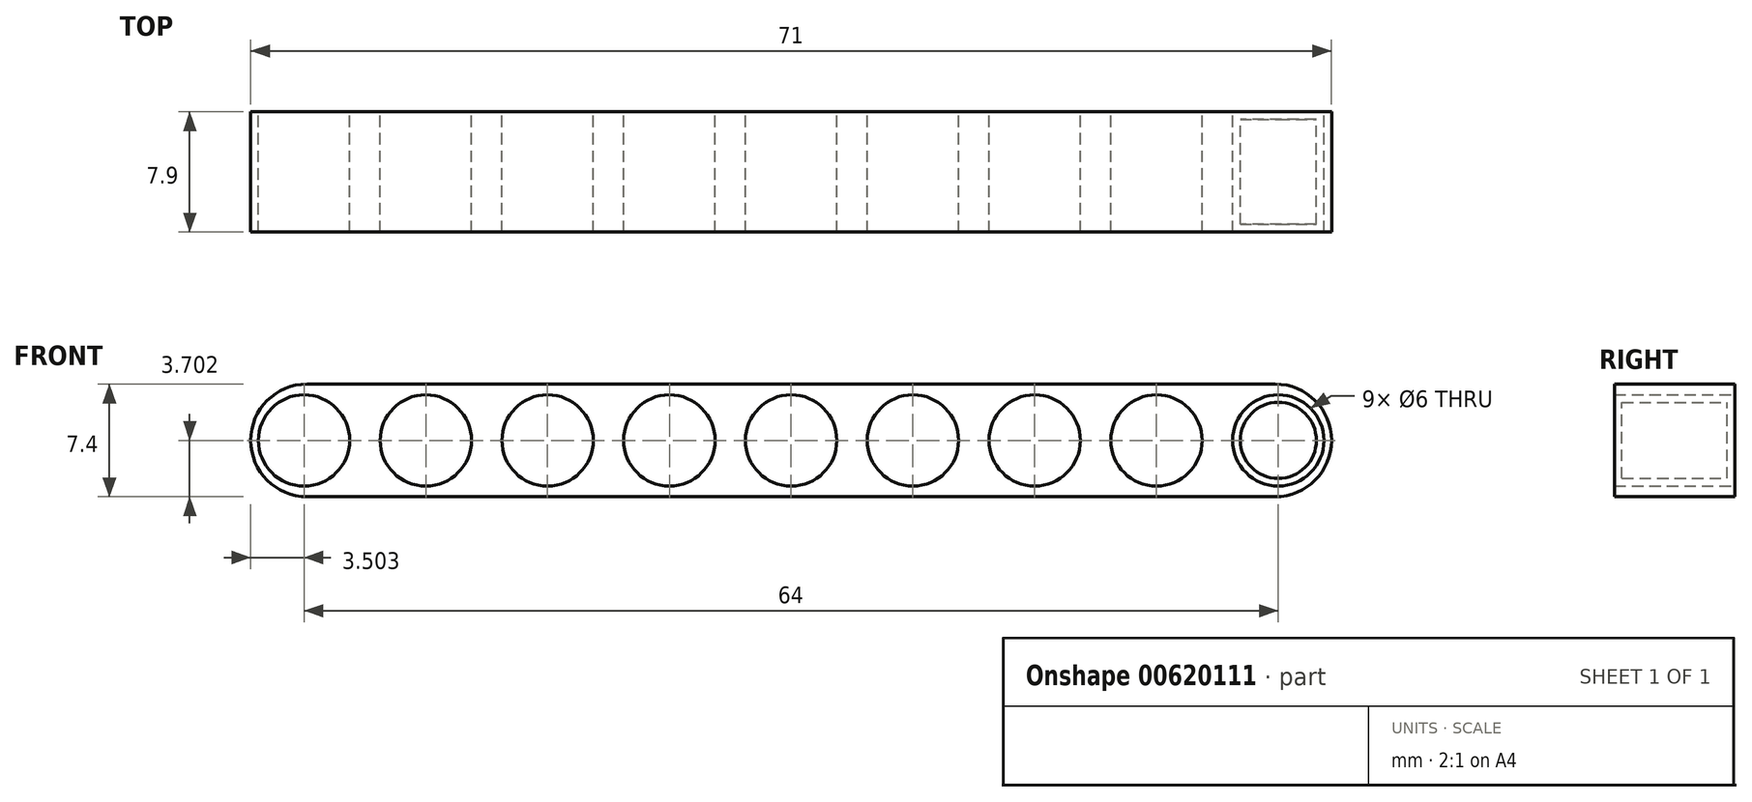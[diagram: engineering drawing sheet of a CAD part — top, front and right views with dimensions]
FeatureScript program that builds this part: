
annotation { "Feature Type Name" : "Feature", "Feature Type Description" : "" }
export const myFeature = defineFeature(function(context is Context, id is Id, definition is map)
    precondition{}
    {
        {
            var Q0;
            Q0=qCreatedBy(makeId("Front.planeOp"),FACE);
            var sketch = newSketch(context, id + "F0", { "sketchPlane" : qUnion([Q0])});
            skLineSegment(sketch, "E0", {"start": v(-49.65, -11.19) * mm, "end": v(-49.65, -18.59) * mm});
            skLineSegment(sketch, "E1", {"start": v(-49.65, -11.19) * mm, "end": v(21.35, -11.19) * mm});
            skLineSegment(sketch, "E2", {"start": v(-49.65, -18.59) * mm, "end": v(21.35, -18.59) * mm});
            skLineSegment(sketch, "E3", {"start": v(21.35, -18.59) * mm, "end": v(21.35, -11.19) * mm});
            skLineSegment(sketch, "E4", {"start": v(-49.65, -14.89) * mm, "end": v(21.35, -14.89) * mm});
            skLineSegment(sketch, "E5", {"start": v(-49.65, -14.89) * mm, "end": v(-46.15, -14.89) * mm});
            skCircle(sketch, "E6", {"center": v(-46.15, -14.89) * mm, "radius": 2.5 * mm});
            skCircle(sketch, "E7", {"center": v(-46.15, -14.89) * mm, "radius": 3 * mm});
            skLineSegment(sketch, "E8", {"start": v(-46.15, -14.89) * mm, "end": v(-38.15, -14.89) * mm});
            skCircle(sketch, "E9", {"center": v(-38.15, -14.89) * mm, "radius": 2.5 * mm});
            skCircle(sketch, "E10", {"center": v(-38.15, -14.89) * mm, "radius": 3 * mm});
            skLineSegment(sketch, "E11", {"start": v(-38.15, -14.89) * mm, "end": v(-30.15, -14.89) * mm});
            skCircle(sketch, "E12", {"center": v(-30.15, -14.89) * mm, "radius": 2.5 * mm});
            skCircle(sketch, "E13", {"center": v(-30.15, -14.89) * mm, "radius": 3 * mm});
            skLineSegment(sketch, "E14", {"start": v(-30.15, -14.89) * mm, "end": v(-22.15, -14.89) * mm});
            skCircle(sketch, "E15", {"center": v(-22.15, -14.89) * mm, "radius": 2.5 * mm});
            skCircle(sketch, "E16", {"center": v(-22.15, -14.89) * mm, "radius": 3 * mm});
            skLineSegment(sketch, "E17", {"start": v(-22.15, -14.89) * mm, "end": v(-14.15, -14.89) * mm});
            skCircle(sketch, "E18", {"center": v(-14.15, -14.89) * mm, "radius": 2.5 * mm});
            skCircle(sketch, "E19", {"center": v(-14.15, -14.89) * mm, "radius": 3 * mm});
            skLineSegment(sketch, "E20", {"start": v(-14.15, -14.89) * mm, "end": v(-6.15, -14.89) * mm});
            skCircle(sketch, "E21", {"center": v(-6.15, -14.89) * mm, "radius": 2.5 * mm});
            skCircle(sketch, "E22", {"center": v(-6.15, -14.89) * mm, "radius": 3 * mm});
            skLineSegment(sketch, "E23", {"start": v(-6.15, -14.89) * mm, "end": v(1.85, -14.89) * mm});
            skCircle(sketch, "E24", {"center": v(1.85, -14.89) * mm, "radius": 2.5 * mm});
            skCircle(sketch, "E25", {"center": v(1.85, -14.89) * mm, "radius": 3 * mm});
            skLineSegment(sketch, "E26", {"start": v(1.85, -14.89) * mm, "end": v(9.85, -14.89) * mm});
            skCircle(sketch, "E27", {"center": v(9.85, -14.89) * mm, "radius": 2.5 * mm});
            skCircle(sketch, "E28", {"center": v(9.85, -14.89) * mm, "radius": 3 * mm});
            skLineSegment(sketch, "E29", {"start": v(9.85, -14.89) * mm, "end": v(17.85, -14.89) * mm});
            skCircle(sketch, "E30", {"center": v(17.85, -14.89) * mm, "radius": 2.5 * mm});
            skCircle(sketch, "E31", {"center": v(17.85, -14.89) * mm, "radius": 3 * mm});
            skSolve(sketch);
        }
        {
            var Q0;
            {var subQ14=sQuery(id+"F0.wireOp",EDGE,"E1");Q0=makeQuery(id+"F0.imprint","IMPRINT",FACE,{"disambiguationData":[TD([[makeQuery(id+"F0.imprint","IMPRINT",EDGE,{"derivedFrom":subQ14}),-1.0]])]});}
            var Q1;
            {var subQ8=sQuery(id+"F0.wireOp",EDGE,"E2");Q1=makeQuery(id+"F0.imprint","IMPRINT",FACE,{"disambiguationData":[TD([[makeQuery(id+"F0.imprint","IMPRINT",EDGE,{"derivedFrom":subQ8}),1.0]])]});}
            extrude(context, id + "F1", {"entities" : qUnion([Q0, Q1]), "endBound" : BoundingType.SYMMETRIC, "depth" : 7.9 * mm, "offsetDistance" : 25 * mm});
        }
        {
            var Q0;
            {var subQ0=sQuery(id+"F0.wireOp",EDGE,"E7");var subQ1=sQuery(id+"F0.wireOp",EDGE,"E5");var subQ2=makeQuery(id+"F0.imprint","INTERSECT",VERTEX,{"derivedFrom":[subQ1,subQ0]});Q0=makeQuery(id+"F0.imprint","IMPRINT",FACE,{"disambiguationData":[TD([[makeQuery(id+"F0.imprint","IMPRINT",EDGE,{"disambiguationData":[TD([[subQ2,-1.0]])],"derivedFrom":subQ1}),1.0]])]});}
            var Q1;
            {var subQ0=sQuery(id+"F0.wireOp",EDGE,"E7");var subQ1=sQuery(id+"F0.wireOp",EDGE,"E5");var subQ2=makeQuery(id+"F0.imprint","INTERSECT",VERTEX,{"derivedFrom":[subQ1,subQ0]});Q1=makeQuery(id+"F0.imprint","IMPRINT",FACE,{"disambiguationData":[TD([[makeQuery(id+"F0.imprint","IMPRINT",EDGE,{"disambiguationData":[TD([[subQ2,-1.0]])],"derivedFrom":subQ1}),-1.0]])]});}
            var Q2;
            {var subQ0=sQuery(id+"F0.wireOp",EDGE,"E10");var subQ1=sQuery(id+"F0.wireOp",EDGE,"E8");var subQ2=makeQuery(id+"F0.imprint","INTERSECT",VERTEX,{"derivedFrom":[subQ1,subQ0]});Q2=makeQuery(id+"F0.imprint","IMPRINT",FACE,{"disambiguationData":[TD([[makeQuery(id+"F0.imprint","IMPRINT",EDGE,{"disambiguationData":[TD([[subQ2,-1.0]])],"derivedFrom":subQ1}),1.0]])]});}
            var Q3;
            {var subQ0=sQuery(id+"F0.wireOp",EDGE,"E10");var subQ1=sQuery(id+"F0.wireOp",EDGE,"E8");var subQ2=makeQuery(id+"F0.imprint","INTERSECT",VERTEX,{"derivedFrom":[subQ1,subQ0]});Q3=makeQuery(id+"F0.imprint","IMPRINT",FACE,{"disambiguationData":[TD([[makeQuery(id+"F0.imprint","IMPRINT",EDGE,{"disambiguationData":[TD([[subQ2,-1.0]])],"derivedFrom":subQ1}),-1.0]])]});}
            var Q4;
            {var subQ0=sQuery(id+"F0.wireOp",EDGE,"E13");var subQ1=sQuery(id+"F0.wireOp",EDGE,"E11");var subQ2=makeQuery(id+"F0.imprint","INTERSECT",VERTEX,{"derivedFrom":[subQ1,subQ0]});Q4=makeQuery(id+"F0.imprint","IMPRINT",FACE,{"disambiguationData":[TD([[makeQuery(id+"F0.imprint","IMPRINT",EDGE,{"disambiguationData":[TD([[subQ2,-1.0]])],"derivedFrom":subQ1}),1.0]])]});}
            var Q5;
            {var subQ0=sQuery(id+"F0.wireOp",EDGE,"E13");var subQ1=sQuery(id+"F0.wireOp",EDGE,"E11");var subQ2=makeQuery(id+"F0.imprint","INTERSECT",VERTEX,{"derivedFrom":[subQ1,subQ0]});Q5=makeQuery(id+"F0.imprint","IMPRINT",FACE,{"disambiguationData":[TD([[makeQuery(id+"F0.imprint","IMPRINT",EDGE,{"disambiguationData":[TD([[subQ2,-1.0]])],"derivedFrom":subQ1}),-1.0]])]});}
            var Q6;
            {var subQ0=sQuery(id+"F0.wireOp",EDGE,"E16");var subQ1=sQuery(id+"F0.wireOp",EDGE,"E14");var subQ2=makeQuery(id+"F0.imprint","INTERSECT",VERTEX,{"derivedFrom":[subQ1,subQ0]});Q6=makeQuery(id+"F0.imprint","IMPRINT",FACE,{"disambiguationData":[TD([[makeQuery(id+"F0.imprint","IMPRINT",EDGE,{"disambiguationData":[TD([[subQ2,-1.0]])],"derivedFrom":subQ1}),1.0]])]});}
            var Q7;
            {var subQ0=sQuery(id+"F0.wireOp",EDGE,"E16");var subQ1=sQuery(id+"F0.wireOp",EDGE,"E14");var subQ2=makeQuery(id+"F0.imprint","INTERSECT",VERTEX,{"derivedFrom":[subQ1,subQ0]});Q7=makeQuery(id+"F0.imprint","IMPRINT",FACE,{"disambiguationData":[TD([[makeQuery(id+"F0.imprint","IMPRINT",EDGE,{"disambiguationData":[TD([[subQ2,-1.0]])],"derivedFrom":subQ1}),-1.0]])]});}
            var Q8;
            {var subQ0=sQuery(id+"F0.wireOp",EDGE,"E19");var subQ1=sQuery(id+"F0.wireOp",EDGE,"E17");var subQ2=makeQuery(id+"F0.imprint","INTERSECT",VERTEX,{"derivedFrom":[subQ1,subQ0]});Q8=makeQuery(id+"F0.imprint","IMPRINT",FACE,{"disambiguationData":[TD([[makeQuery(id+"F0.imprint","IMPRINT",EDGE,{"disambiguationData":[TD([[subQ2,-1.0]])],"derivedFrom":subQ1}),-1.0]])]});}
            var Q9;
            {var subQ0=sQuery(id+"F0.wireOp",EDGE,"E19");var subQ1=sQuery(id+"F0.wireOp",EDGE,"E17");var subQ2=makeQuery(id+"F0.imprint","INTERSECT",VERTEX,{"derivedFrom":[subQ1,subQ0]});Q9=makeQuery(id+"F0.imprint","IMPRINT",FACE,{"disambiguationData":[TD([[makeQuery(id+"F0.imprint","IMPRINT",EDGE,{"disambiguationData":[TD([[subQ2,-1.0]])],"derivedFrom":subQ1}),1.0]])]});}
            var Q10;
            {var subQ0=sQuery(id+"F0.wireOp",EDGE,"E22");var subQ1=sQuery(id+"F0.wireOp",EDGE,"E20");var subQ2=makeQuery(id+"F0.imprint","INTERSECT",VERTEX,{"derivedFrom":[subQ1,subQ0]});Q10=makeQuery(id+"F0.imprint","IMPRINT",FACE,{"disambiguationData":[TD([[makeQuery(id+"F0.imprint","IMPRINT",EDGE,{"disambiguationData":[TD([[subQ2,-1.0]])],"derivedFrom":subQ1}),1.0]])]});}
            var Q11;
            {var subQ0=sQuery(id+"F0.wireOp",EDGE,"E22");var subQ1=sQuery(id+"F0.wireOp",EDGE,"E20");var subQ2=makeQuery(id+"F0.imprint","INTERSECT",VERTEX,{"derivedFrom":[subQ1,subQ0]});Q11=makeQuery(id+"F0.imprint","IMPRINT",FACE,{"disambiguationData":[TD([[makeQuery(id+"F0.imprint","IMPRINT",EDGE,{"disambiguationData":[TD([[subQ2,-1.0]])],"derivedFrom":subQ1}),-1.0]])]});}
            var Q12;
            {var subQ0=sQuery(id+"F0.wireOp",EDGE,"E25");var subQ1=sQuery(id+"F0.wireOp",EDGE,"E23");var subQ2=makeQuery(id+"F0.imprint","INTERSECT",VERTEX,{"derivedFrom":[subQ1,subQ0]});Q12=makeQuery(id+"F0.imprint","IMPRINT",FACE,{"disambiguationData":[TD([[makeQuery(id+"F0.imprint","IMPRINT",EDGE,{"disambiguationData":[TD([[subQ2,-1.0]])],"derivedFrom":subQ1}),1.0]])]});}
            var Q13;
            {var subQ0=sQuery(id+"F0.wireOp",EDGE,"E25");var subQ1=sQuery(id+"F0.wireOp",EDGE,"E23");var subQ2=makeQuery(id+"F0.imprint","INTERSECT",VERTEX,{"derivedFrom":[subQ1,subQ0]});Q13=makeQuery(id+"F0.imprint","IMPRINT",FACE,{"disambiguationData":[TD([[makeQuery(id+"F0.imprint","IMPRINT",EDGE,{"disambiguationData":[TD([[subQ2,-1.0]])],"derivedFrom":subQ1}),-1.0]])]});}
            var Q14;
            {var subQ0=sQuery(id+"F0.wireOp",EDGE,"E28");var subQ1=sQuery(id+"F0.wireOp",EDGE,"E26");var subQ2=makeQuery(id+"F0.imprint","INTERSECT",VERTEX,{"derivedFrom":[subQ1,subQ0]});Q14=makeQuery(id+"F0.imprint","IMPRINT",FACE,{"disambiguationData":[TD([[makeQuery(id+"F0.imprint","IMPRINT",EDGE,{"disambiguationData":[TD([[subQ2,-1.0]])],"derivedFrom":subQ1}),1.0]])]});}
            var Q15;
            {var subQ0=sQuery(id+"F0.wireOp",EDGE,"E28");var subQ1=sQuery(id+"F0.wireOp",EDGE,"E26");var subQ2=makeQuery(id+"F0.imprint","INTERSECT",VERTEX,{"derivedFrom":[subQ1,subQ0]});Q15=makeQuery(id+"F0.imprint","IMPRINT",FACE,{"disambiguationData":[TD([[makeQuery(id+"F0.imprint","IMPRINT",EDGE,{"disambiguationData":[TD([[subQ2,-1.0]])],"derivedFrom":subQ1}),-1.0]])]});}
            var Q16;
            {var subQ0=sQuery(id+"F0.wireOp",EDGE,"E30");var subQ1=sQuery(id+"F0.wireOp",EDGE,"E4");var subQ2=makeQuery(id+"F0.imprint","INTERSECT",VERTEX,{"derivedFrom":[subQ1,subQ0]});Q16=makeQuery(id+"F0.imprint","IMPRINT",FACE,{"disambiguationData":[TD([[makeQuery(id+"F0.imprint","IMPRINT",EDGE,{"disambiguationData":[TD([[subQ2,-1.0]])],"derivedFrom":subQ1}),1.0]])]});}
            var Q17;
            {var subQ0=sQuery(id+"F0.wireOp",EDGE,"E30");var subQ1=sQuery(id+"F0.wireOp",EDGE,"E4");var subQ2=makeQuery(id+"F0.imprint","INTERSECT",VERTEX,{"derivedFrom":[subQ1,subQ0]});Q17=makeQuery(id+"F0.imprint","IMPRINT",FACE,{"disambiguationData":[TD([[makeQuery(id+"F0.imprint","IMPRINT",EDGE,{"disambiguationData":[TD([[subQ2,-1.0]])],"derivedFrom":subQ1}),-1.0]])]});}
            extrude(context, id + "F2", {"entities" : qUnion([Q0, Q1, Q2, Q3, Q4, Q5, Q6, Q7, Q8, Q9, Q10, Q11, Q12, Q13, Q14, Q15, Q16, Q17]), "operationType" : NewBodyOperationType.ADD, "endBound" : BoundingType.SYMMETRIC, "depth" : 6.9 * mm, "offsetDistance" : 25 * mm});
        }
        {
            var Q0;
            Q0=makeQuery(id+"F1.opExtrude","SWEPT_EDGE",EDGE,{"disambiguationData":[OSD([sQuery(id+"F0.wireOp",EDGE,"E1"),sQuery(id+"F0.wireOp",EDGE,"E3")])]});
            var Q1;
            Q1=makeQuery(id+"F1.opExtrude","SWEPT_EDGE",EDGE,{"disambiguationData":[OSD([sQuery(id+"F0.wireOp",EDGE,"E2"),sQuery(id+"F0.wireOp",EDGE,"E3")])]});
            var Q2;
            Q2=makeQuery(id+"F1.opExtrude","SWEPT_EDGE",EDGE,{"disambiguationData":[OSD([sQuery(id+"F0.wireOp",EDGE,"E0"),sQuery(id+"F0.wireOp",EDGE,"E1")])]});
            var Q3;
            Q3=makeQuery(id+"F1.opExtrude","SWEPT_EDGE",EDGE,{"disambiguationData":[OSD([sQuery(id+"F0.wireOp",EDGE,"E0"),sQuery(id+"F0.wireOp",EDGE,"E2")])]});
            fillet(context, id + "F3", {"entities" : qUnion([Q0, Q1, Q2, Q3]), "radius" : 3.7 * mm, "tangentPropagation" : true, "allowEdgeOverflow" : false});
        }
    });
